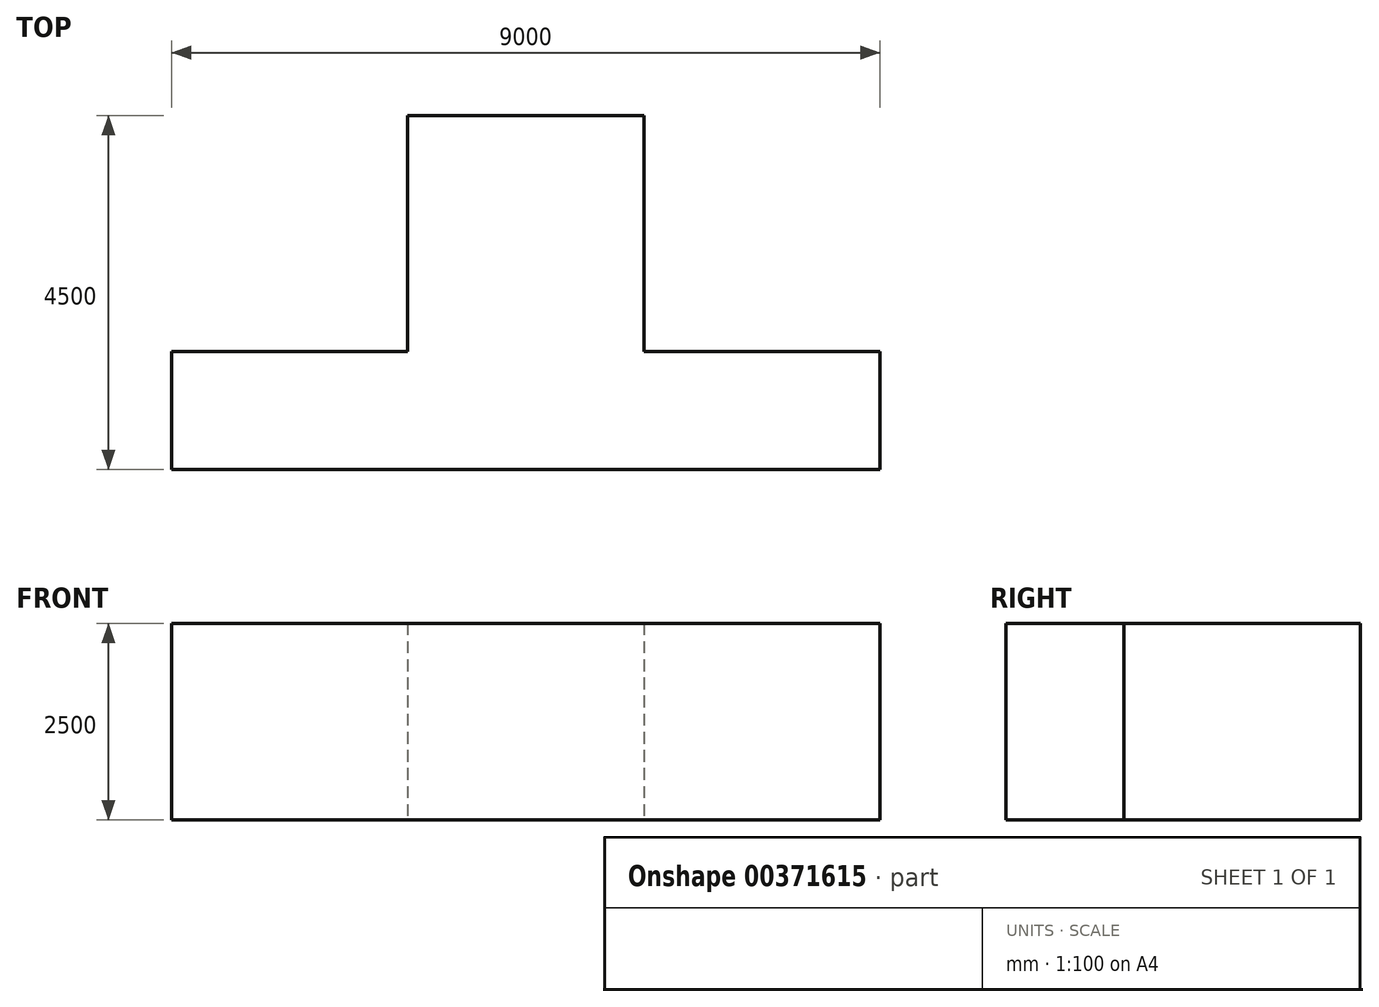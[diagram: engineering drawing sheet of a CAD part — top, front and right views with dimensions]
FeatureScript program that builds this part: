
annotation { "Feature Type Name" : "Feature", "Feature Type Description" : "" }
export const myFeature = defineFeature(function(context is Context, id is Id, definition is map)
    precondition{}
    {
        {
            var Q0;
            Q0=qCreatedBy(makeId("Top.planeOp"),FACE);
            var sketch = newSketch(context, id + "F0", { "sketchPlane" : qUnion([Q0])});
            skLineSegment(sketch, "E0", {"start": v(6000, -4500) * mm, "end": v(-3000, -4500) * mm});
            skLineSegment(sketch, "E1", {"start": v(-3000, -4500) * mm, "end": v(-3000, -3000) * mm});
            skLineSegment(sketch, "E2", {"start": v(-3000, -3000) * mm, "end": v(0, -3000) * mm});
            skLineSegment(sketch, "E3", {"start": v(0, -3000) * mm, "end": v(0, 0) * mm});
            skLineSegment(sketch, "E4", {"start": v(0, 0) * mm, "end": v(3000, 0) * mm});
            skLineSegment(sketch, "E5", {"start": v(3000, 0) * mm, "end": v(3000, -3000) * mm});
            skLineSegment(sketch, "E6", {"start": v(3000, -3000) * mm, "end": v(6000, -3000) * mm});
            skLineSegment(sketch, "E7", {"start": v(6000, -3000) * mm, "end": v(6000, -4500) * mm});
            skSolve(sketch);
        }
        {
            var Q0;
            Q0 = qSketchRegion(id + "F0", true);
            extrude(context, id + "F1", {"entities" : qUnion([Q0]), "depth" : 2500 * mm, "offsetDistance" : 25 * mm});
        }
    });
